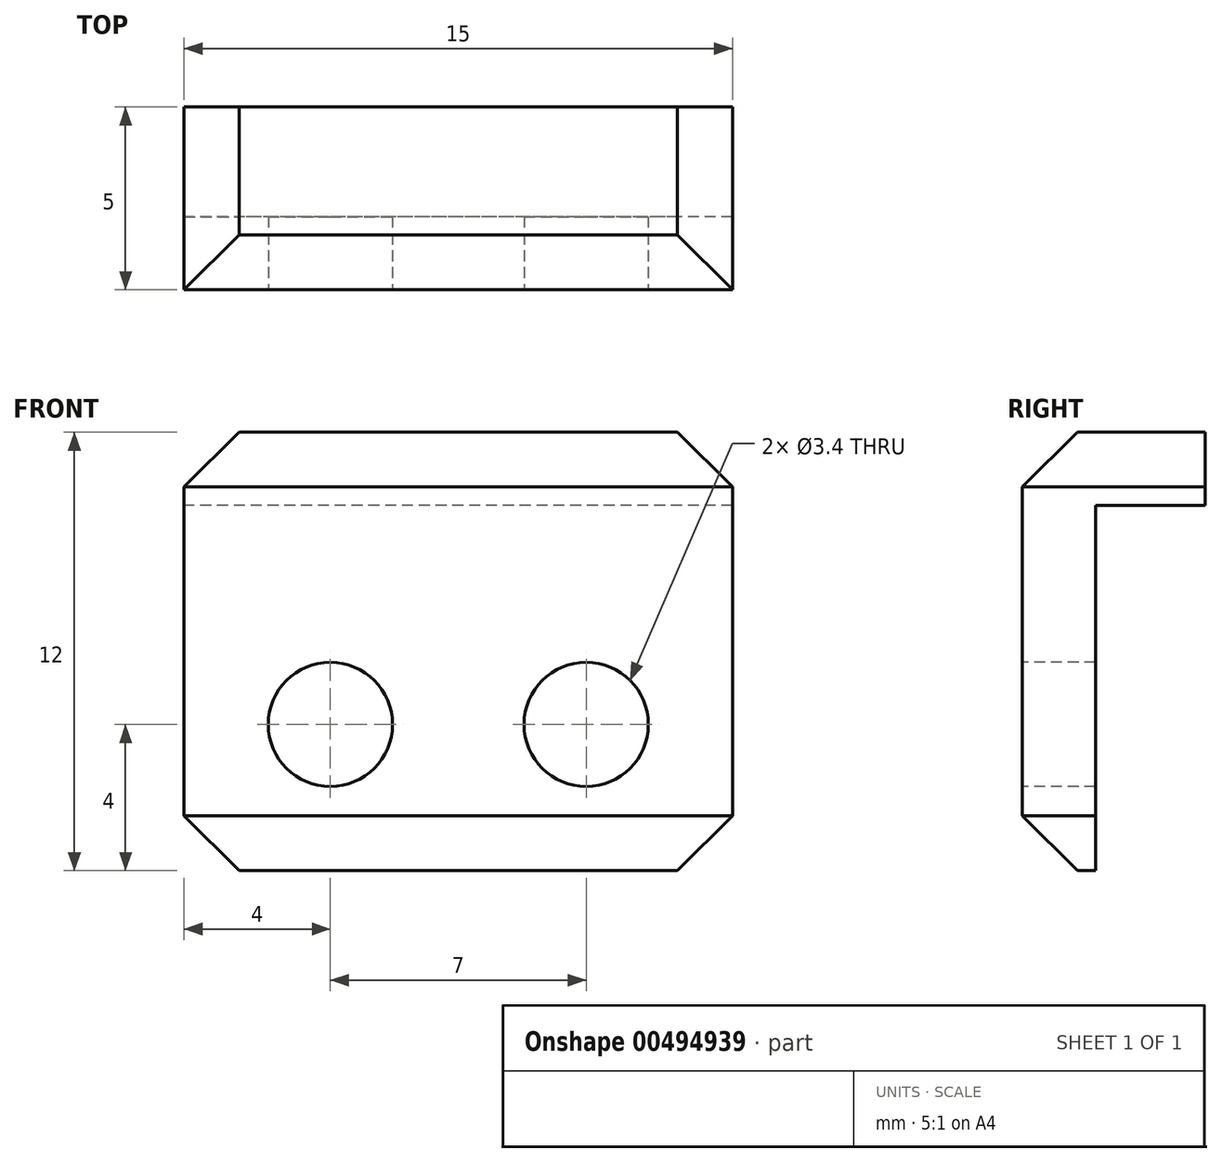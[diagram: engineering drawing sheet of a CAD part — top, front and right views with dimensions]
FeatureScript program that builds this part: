
annotation { "Feature Type Name" : "Feature", "Feature Type Description" : "" }
export const myFeature = defineFeature(function(context is Context, id is Id, definition is map)
    precondition{}
    {
        {
            var Q0;
            Q0=qCreatedBy(makeId("Right.planeOp"),FACE);
            var sketch = newSketch(context, id + "F0", { "sketchPlane" : qUnion([Q0])});
            skLineSegment(sketch, "E0", {"start": v(0, 0) * mm, "end": v(3, 0) * mm});
            skLineSegment(sketch, "E1", {"start": v(3, 0) * mm, "end": v(3, 2) * mm});
            skLineSegment(sketch, "E2", {"start": v(3, 2) * mm, "end": v(-2, 2) * mm});
            skLineSegment(sketch, "E3", {"start": v(-2, 2) * mm, "end": v(-2, -10) * mm});
            skLineSegment(sketch, "E4", {"start": v(-2, -10) * mm, "end": v(0, -10) * mm});
            skLineSegment(sketch, "E5", {"start": v(0, -10) * mm, "end": v(0, 0) * mm});
            skSolve(sketch);
        }
        {
            var Q0;
            Q0=qSketchRegion(id+"F0",true);
            extrude(context, id + "F1", {"entities" : qUnion([Q0]), "depth" : 15 * mm});
        }
        {
            var Q0;
            Q0=makeQuery(id+"F1.opExtrude","SWEPT_FACE",FACE,{"disambiguationData":[OSD([sQuery(id+"F0.wireOp",EDGE,"E3")])]});
            var sketch = newSketch(context, id + "F2", { "sketchPlane" : qUnion([Q0])});
            skPoint(sketch, "E6", {"position": v(4, -6) * mm});
            skPoint(sketch, "E7", {"position": v(11, -6) * mm});
            skSolve(sketch);
        }
        {
            var Q0;
            Q0=sQuery(id+"F2.wireOp",VERTEX,"E6");
            var Q1;
            Q1=sQuery(id+"F2.wireOp",VERTEX,"E7");
            var Q2;
            Q2=makeQuery(id+"F1.opExtrude","SWEPT_BODY",BODY,{"disambiguationData":[OSD([sQuery(id+"F0.wireOp",EDGE,"E0"),sQuery(id+"F0.wireOp",EDGE,"E1"),sQuery(id+"F0.wireOp",EDGE,"E2"),sQuery(id+"F0.wireOp",EDGE,"E3"),sQuery(id+"F0.wireOp",EDGE,"E4"),sQuery(id+"F0.wireOp",EDGE,"E5")])]});
            hole(context, id + "F3", {"style" : HoleStyle.SIMPLE, "endStyle" : HoleEndStyle.THROUGH, "standardTappedOrClearance" : lookupTablePath({ "standard" : "ISO", "size" : "3.4", "type" : "Drilled" }), "standardBlindInLast" : lookupTablePath({ "standard" : "ISO", "size" : "3.4", "type" : "Drilled" }), "holeDiameter" : 3.4 * mm, "isTappedThrough" : true, "tappedDepth" : 12 * mm, "tapClearance" : 3, "locations" : qUnion([Q0, Q1]), "scope" : qUnion([Q2])});
        }
        {
            var Q0;
            Q0=makeQuery(id+"F1.opExtrude","CAP_EDGE",EDGE,{"disambiguationData":[OSD([sQuery(id+"F0.wireOp",EDGE,"E2")])],"isStart":true});
            var Q1;
            Q1=makeQuery(id+"F1.opExtrude","CAP_EDGE",EDGE,{"disambiguationData":[OSD([sQuery(id+"F0.wireOp",EDGE,"E2")])],"isStart":false});
            var Q2;
            Q2=makeQuery(id+"F1.opExtrude","CAP_EDGE",EDGE,{"disambiguationData":[OSD([sQuery(id+"F0.wireOp",EDGE,"E4")])],"isStart":true});
            var Q3;
            Q3=makeQuery(id+"F1.opExtrude","CAP_EDGE",EDGE,{"disambiguationData":[OSD([sQuery(id+"F0.wireOp",EDGE,"E4")])],"isStart":false});
            var Q4;
            Q4=makeQuery(id+"F1.opExtrude","SWEPT_EDGE",EDGE,{"disambiguationData":[OSD([sQuery(id+"F0.wireOp",EDGE,"E2"),sQuery(id+"F0.wireOp",EDGE,"E3")])]});
            var Q5;
            Q5=makeQuery(id+"F1.opExtrude","SWEPT_EDGE",EDGE,{"disambiguationData":[OSD([sQuery(id+"F0.wireOp",EDGE,"E3"),sQuery(id+"F0.wireOp",EDGE,"E4")])]});
            chamfer(context, id + "F4", {"entities" : qUnion([Q0, Q1, Q2, Q3, Q4, Q5]), "width" : 1.5 * mm, "tangentPropagation" : true});
        }
    });
